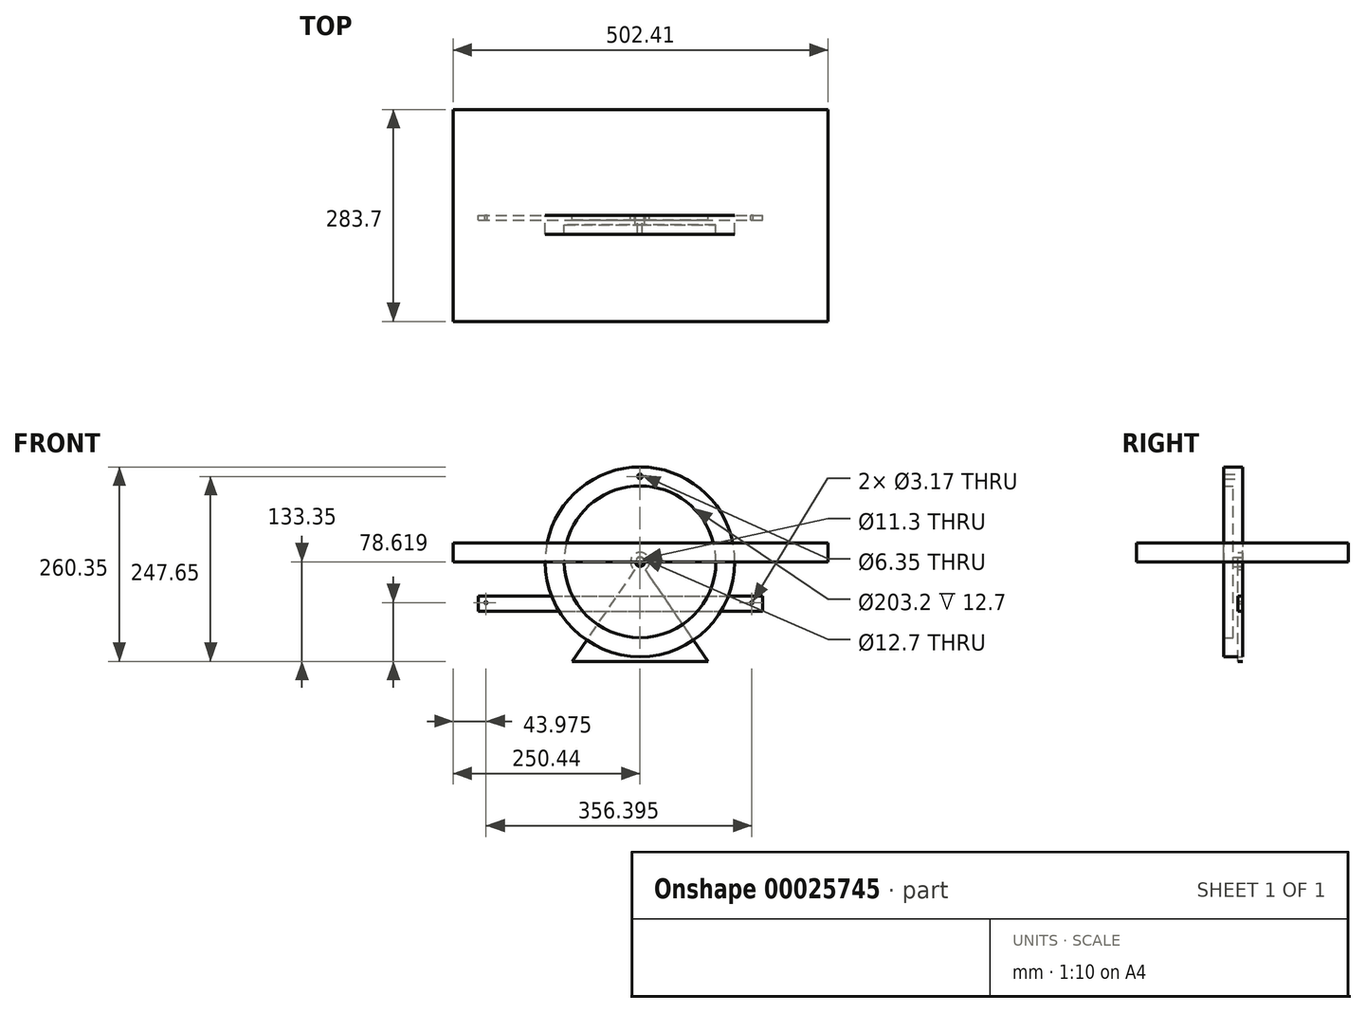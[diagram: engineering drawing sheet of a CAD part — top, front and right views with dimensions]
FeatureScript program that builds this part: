
annotation { "Feature Type Name" : "Feature", "Feature Type Description" : "" }
export const myFeature = defineFeature(function(context is Context, id is Id, definition is map)
    precondition{}
    {
        {
            var Q0;
            Q0=qCreatedBy(makeId("Front.planeOp"),FACE);
            var sketch = newSketch(context, id + "F0", { "sketchPlane" : qUnion([Q0])});
            skCircle(sketch, "E0", {"center": v(0, 0) * mm, "radius": 101.6 * mm});
            skCircle(sketch, "E1", {"center": v(0, 0) * mm, "radius": 127 * mm});
            skCircle(sketch, "E2", {"center": v(0, 0) * mm, "radius": 6.35 * mm});
            skCircle(sketch, "E3", {"center": v(0, 114.3) * mm, "radius": 3.18 * mm});
            skSolve(sketch);
        }
        {
            var Q0;
            Q0=makeQuery(id+"F0.imprint","IMPRINT",FACE,{"disambiguationData":[TD([[makeQuery(id+"F0.imprint","IMPRINT",EDGE,{"derivedFrom":sQuery(id+"F0.wireOp",EDGE,"E0")}),-1.0]])]});
            var Q1;
            Q1=sQuery(id+"F0.wireOp",EDGE,"E0");
            var Q2;
            Q2=sQuery(id+"F0.wireOp",EDGE,"E1");
            extrude(context, id + "F1", {"entities" : qUnion([Q0]), "surfaceEntities" : qUnion([Q1, Q2]), "depth" : 25.4 * mm});
        }
        {
            var Q0;
            Q0=makeQuery(id+"F0.imprint","IMPRINT",FACE,{"disambiguationData":[TD([[makeQuery(id+"F0.imprint","IMPRINT",EDGE,{"derivedFrom":sQuery(id+"F0.wireOp",EDGE,"E0")}),1.0]])]});
            var Q1;
            Q1=sQuery(id+"F0.wireOp",EDGE,"E0");
            extrude(context, id + "F2", {"entities" : qUnion([Q0]), "operationType" : NewBodyOperationType.ADD, "surfaceEntities" : qUnion([Q1]), "depth" : 12.7 * mm});
        }
        {
            var Q0;
            Q0=qCreatedBy(makeId("Front.planeOp"),FACE);
            var sketch = newSketch(context, id + "F3", { "sketchPlane" : qUnion([Q0])});
            skCircle(sketch, "E4", {"center": v(0, 0) * mm, "radius": 12.7 * mm});
            skLineSegment(sketch, "E5", {"start": v(0, 0) * mm, "end": v(-91.06, -133.35) * mm});
            skLineSegment(sketch, "E6", {"start": v(-91.06, -133.35) * mm, "end": v(91.06, -133.35) * mm});
            skLineSegment(sketch, "E7", {"start": v(91.06, -133.35) * mm, "end": v(0, 0) * mm});
            skCircle(sketch, "E8", {"center": v(0, 0) * mm, "radius": 5.65 * mm});
            skSolve(sketch);
        }
        {
            var Q0;
            {var subQ3=sQuery(id+"F3.wireOp",EDGE,"E6");Q0=makeQuery(id+"F3.imprint","IMPRINT",FACE,{"disambiguationData":[TD([[makeQuery(id+"F3.imprint","IMPRINT",EDGE,{"derivedFrom":subQ3}),1.0]])]});}
            var Q1;
            {var subQ3=sQuery(id+"F3.wireOp",EDGE,"E5");var subQ5=sQuery(id+"F3.wireOp",EDGE,"E4");var subQ7=makeQuery(id+"F3.imprint","INTERSECT",VERTEX,{"derivedFrom":[subQ5,subQ3]});Q1=makeQuery(id+"F3.imprint","IMPRINT",FACE,{"disambiguationData":[TD([[makeQuery(id+"F3.imprint","IMPRINT",EDGE,{"disambiguationData":[TD([[subQ7,1.0]])],"derivedFrom":subQ5}),1.0]])]});}
            var Q2;
            {var subQ3=sQuery(id+"F3.wireOp",EDGE,"E5");var subQ5=sQuery(id+"F3.wireOp",EDGE,"E4");var subQ7=makeQuery(id+"F3.imprint","INTERSECT",VERTEX,{"derivedFrom":[subQ5,subQ3]});Q2=makeQuery(id+"F3.imprint","IMPRINT",FACE,{"disambiguationData":[TD([[makeQuery(id+"F3.imprint","IMPRINT",EDGE,{"disambiguationData":[TD([[subQ7,-1.0]])],"derivedFrom":subQ5}),1.0]])]});}
            extrude(context, id + "F4", {"entities" : qUnion([Q0, Q1, Q2]), "depth" : 6.35 * mm});
        }
        {
            var Q0;
            Q0=qCreatedBy(makeId("Front.planeOp"),FACE);
            var sketch = newSketch(context, id + "F5", { "sketchPlane" : qUnion([Q0])});
            skLineSegment(sketch, "E9.bottom", {"start": v(-216.46, -45.73) * mm, "end": v(164.54, -45.73) * mm});
            skLineSegment(sketch, "E9.top", {"start": v(-216.46, -66.53) * mm, "end": v(164.54, -66.53) * mm});
            skLineSegment(sketch, "E9.left", {"start": v(-216.46, -45.73) * mm, "end": v(-216.46, -66.53) * mm});
            skLineSegment(sketch, "E9.right", {"start": v(164.54, -45.73) * mm, "end": v(164.54, -66.53) * mm});
            skCircle(sketch, "E10", {"center": v(149.93, -54.73) * mm, "radius": 1.59 * mm});
            skCircle(sketch, "E11", {"center": v(-206.46, -54.73) * mm, "radius": 1.59 * mm});
            skSolve(sketch);
        }
        {
            var Q0;
            Q0 = qSketchRegion(id + "F5", true);
            extrude(context, id + "F6", {"entities" : qUnion([Q0]), "depth" : 6.35 * mm});
        }
        {
            var Q0;
            Q0=qCreatedBy(makeId("Top.planeOp"),FACE);
            var sketch = newSketch(context, id + "F7", { "sketchPlane" : qUnion([Q0])});
            skLineSegment(sketch, "E12.bottom", {"start": v(-250.44, 141.47) * mm, "end": v(251.97, 141.47) * mm});
            skLineSegment(sketch, "E12.top", {"start": v(-250.44, -142.23) * mm, "end": v(251.97, -142.23) * mm});
            skLineSegment(sketch, "E12.left", {"start": v(-250.44, 141.47) * mm, "end": v(-250.44, -142.23) * mm});
            skLineSegment(sketch, "E12.right", {"start": v(251.97, 141.47) * mm, "end": v(251.97, -142.23) * mm});
            skSolve(sketch);
        }
        {
            var Q0;
            Q0 = qSketchRegion(id + "F7", true);
            extrude(context, id + "F8", {"entities" : qUnion([Q0]), "depth" : 25.4 * mm});
        }
    });
